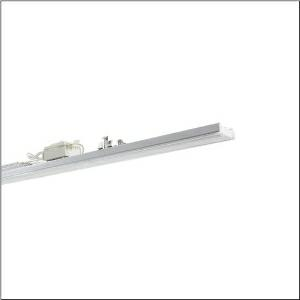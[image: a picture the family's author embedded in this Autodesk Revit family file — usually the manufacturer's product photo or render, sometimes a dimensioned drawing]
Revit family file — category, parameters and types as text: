
# Revit family: licross_r__11_recessed_ho_51tl12dn3dxm_68dd
name_source: partatom
category: Lighting Fixtures
units: mm (PartAtom-declared; Revit-internal decimal feet)

## family parameters
Cut with Voids When Loaded = No
Host = Face
Light Source = No
Part Type = Normal
Room Calculation Point = No
Round Connector Dimension = Use Diameter
Shared = No

## types (1)
- --- (1 x LED, 13490 lm, 76.8 W, 3000K)
    Apparent Load = 77 VA
    CIE Flux Codes = 66 91 98 100 100
    Color Rendering = 80
    Color Temperature = 3000K
    Default Elevation = 1800 mm
    Description = Licross® 11 Recessed HO, luminaire insert, of sheet steel, coil coated, white, length: 1.500mm, width: 66mm, height: 67mm, LED rated luminous flux: 13.490lm, light colour: 830, control gear: DALI 2, with plug, 5-pole, with phase selection, mains connection: 220..240V, AC, 50/60Hz, rated input power: 77W, halogen-free wiring, primary optical cover: cover, of PMMA, light emission: direct distribution, primary light characteristic: symmetric, protection rating (complete): IP40, insulation class (complete): insulation class I (protective earthing), certification: CE, ENEC, VDE, UKCA, protection symbol: D if used in an environment without relevant dust loads with corresponding accessories, impact resistance: IK06, permissible ambient temperature for indoor applications: -25..+30°C, corresponds to IFS (International Featured Standards) requirements for safety and quality in the food industry, reducing of maximum allowable ambient temperature of 5°C with ceiling mounting, LABS conformity tested according to VDMA 24364:2018-05, packaging unit: 1 piece
    Height = 58 mm
    Lamp = 1 x LED
    Lamp Light Flux = 13490 lm
    Lamp Power = 76.8 W
    Lamp count = 1
    Length = 1500 mm
    Luminous efficacy = 176 lm/W
    Manufacturer = Siteco
    ModVariant = No
    Model = 51TL12DN3DXM
    Mounting Place = Ceiling
    Mounting Type = Pendant
    Number of Poles = 1
    OnlyDefault = Yes
    Power Factor = 1
    Product Name = Licross® 11 Recessed HO
    Product group = luminaire insert
    ProductGroupID = 902
    Protection Class = Protection class I
    Protection Degree = IP 40
    RLX_Detail_Level = 1
    RLX_Emergency_Light_Flux = 0 lm
    RLX_Emergency_Type = 0
    RLX_Emergency_Type_DB = No
    RlxData = <blob elided: 24533 chars, md5=63d090f5>
    Socket = socket
    Standby Power = 0 W
    System Light Flux = 13490 lm
    System Power = 77 W
    Type Comments = factory setting: luminous flux: 100 % | dim-lin: 254 | 522 mA
    Type Image = l_1296930.jpg
    URL = http://relux.com
    VarID = @adj_067920
    Voltage = 0 V
    Weight = 0.00 kg
    Width = 66 mm

## geometry (parser evidence)
native form markers: Blend x4, Sweep x12
no freeform markers — native parametric forms only
